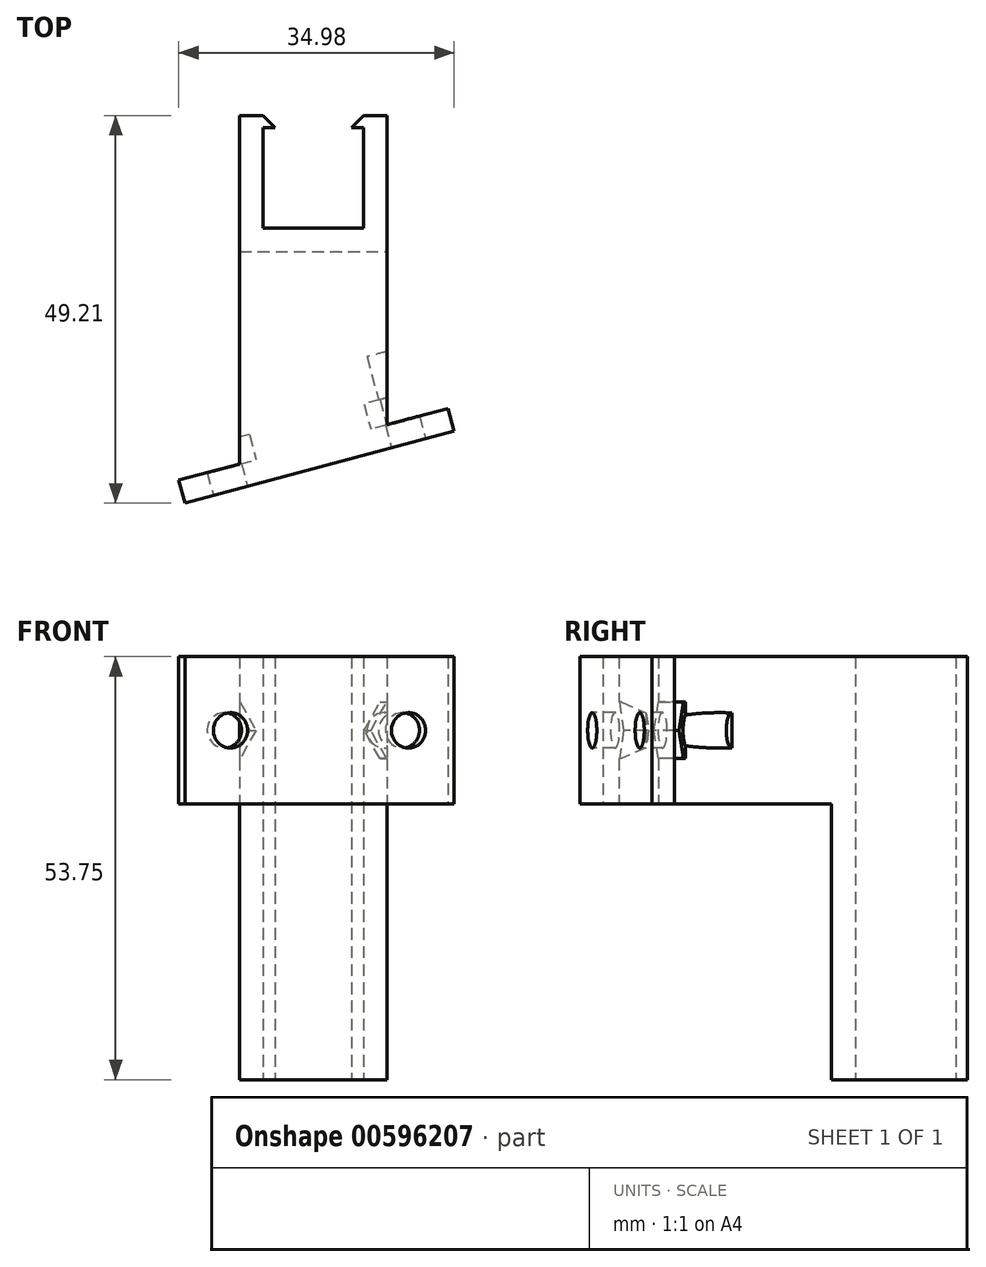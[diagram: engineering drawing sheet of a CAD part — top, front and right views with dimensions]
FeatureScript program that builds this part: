
annotation { "Feature Type Name" : "Feature", "Feature Type Description" : "" }
export const myFeature = defineFeature(function(context is Context, id is Id, definition is map)
    precondition{}
    {
        {
            assignVariable(context, id + "F0", {"name" : "bar", "anyValue" : 12.75});
        }
        {
            assignVariable(context, id + "F1", {"name" : "thickness", "anyValue" : 3});
        }
        {
            var Q0;
            Q0=qCreatedBy(makeId("Top.planeOp"),FACE);
            var sketch = newSketch(context, id + "F2", { "sketchPlane" : qUnion([Q0])});
            skLineSegment(sketch, "E0", {"start": v(-6.69, 24) * mm, "end": v(-6.69, 11.26) * mm});
            skLineSegment(sketch, "E1", {"start": v(-6.69, 11.26) * mm, "end": v(6.06, 11.26) * mm});
            skLineSegment(sketch, "E2", {"start": v(6.06, 11.26) * mm, "end": v(6.06, 24) * mm});
            skLineSegment(sketch, "E3", {"start": v(6.06, 24) * mm, "end": v(9.06, 24) * mm, "construction": true});
            skLineSegment(sketch, "E4", {"start": v(9.06, -13.74) * mm, "end": v(-9.69, -18.74) * mm});
            skLineSegment(sketch, "E5", {"start": v(-9.69, 24) * mm, "end": v(-6.69, 24) * mm, "construction": true});
            skLineSegment(sketch, "E6", {"start": v(6.06, 11.26) * mm, "end": v(9.06, 11.26) * mm, "construction": true});
            skLineSegment(sketch, "E7", {"start": v(-6.69, 11.26) * mm, "end": v(-9.69, 11.26) * mm, "construction": true});
            skLineSegment(sketch, "E8", {"start": v(9.06, 24) * mm, "end": v(9.06, 11.26) * mm});
            skLineSegment(sketch, "E9", {"start": v(9.06, 11.26) * mm, "end": v(9.06, -13.74) * mm});
            skLineSegment(sketch, "E10", {"start": v(-9.69, 11.26) * mm, "end": v(-9.69, -18.74) * mm});
            skLineSegment(sketch, "E11", {"start": v(-9.69, 11.26) * mm, "end": v(-9.69, 24) * mm});
            skLineSegment(sketch, "E12", {"start": v(-6.69, 24) * mm, "end": v(-5.19, 24) * mm});
            skLineSegment(sketch, "E13", {"start": v(-5.19, 24) * mm, "end": v(-6.69, 25.5) * mm});
            skLineSegment(sketch, "E14", {"start": v(-6.69, 25.5) * mm, "end": v(-9.69, 25.5) * mm});
            skLineSegment(sketch, "E15", {"start": v(-9.69, 25.5) * mm, "end": v(-9.69, 24) * mm});
            skLineSegment(sketch, "E16", {"start": v(6.06, 24) * mm, "end": v(4.56, 24) * mm});
            skLineSegment(sketch, "E17", {"start": v(4.56, 24) * mm, "end": v(6.06, 25.5) * mm});
            skLineSegment(sketch, "E18", {"start": v(6.06, 25.5) * mm, "end": v(9.06, 25.5) * mm});
            skLineSegment(sketch, "E19", {"start": v(9.06, 25.5) * mm, "end": v(9.06, 24) * mm});
            skSolve(sketch);
        }
        {
            var Q0;
            Q0=makeQuery(id+"F2.imprint","IMPRINT",FACE,{"disambiguationData":[TD([[makeQuery(id+"F2.imprint","IMPRINT",EDGE,{"derivedFrom":sQuery(id+"F2.wireOp",EDGE,"E0")}),-1.0]])]});
            extrude(context, id + "F3", {"entities" : qUnion([Q0]), "depth" : (2 * getVariable(context, 'thickness') + getVariable(context, 'bar')) * mm, "offsetDistance" : 25 * mm});
        }
        {
            var Q0;
            Q0=makeQuery(id+"F3.opExtrude","SWEPT_FACE",FACE,{"disambiguationData":[OSD([sQuery(id+"F2.wireOp",EDGE,"E4")])]});
            var sketch = newSketch(context, id + "F4", { "sketchPlane" : qUnion([Q0])});
            skLineSegment(sketch, "E20.bottom", {"start": v(-14.2, 18.75) * mm, "end": v(-22.2, 18.75) * mm});
            skLineSegment(sketch, "E20.top", {"start": v(-14.2, 0) * mm, "end": v(-22.2, 0) * mm});
            skLineSegment(sketch, "E20.left", {"start": v(-14.2, 18.75) * mm, "end": v(-14.2, 0) * mm});
            skLineSegment(sketch, "E20.right", {"start": v(-22.2, 18.75) * mm, "end": v(-22.2, 0) * mm});
            skLineSegment(sketch, "E21.bottom", {"start": v(5.21, 18.75) * mm, "end": v(13.21, 18.75) * mm});
            skLineSegment(sketch, "E21.top", {"start": v(5.21, 0) * mm, "end": v(13.21, 0) * mm});
            skLineSegment(sketch, "E21.left", {"start": v(5.21, 18.75) * mm, "end": v(5.21, 0) * mm});
            skLineSegment(sketch, "E21.right", {"start": v(13.21, 18.75) * mm, "end": v(13.21, 0) * mm});
            skLineSegment(sketch, "E22.bottom", {"start": v(5.21, 18.75) * mm, "end": v(-14.2, 18.75) * mm});
            skLineSegment(sketch, "E22.top", {"start": v(5.21, 0) * mm, "end": v(-14.2, 0) * mm});
            skSolve(sketch);
        }
        {
            var Q0;
            Q0=makeQuery(id+"F4.imprint","IMPRINT",FACE,{"disambiguationData":[TD([[makeQuery(id+"F4.imprint","IMPRINT",EDGE,{"derivedFrom":sQuery(id+"F4.wireOp",EDGE,"E22.bottom")}),1.0]])]});
            var Q1;
            Q1=makeQuery(id+"F4.imprint","IMPRINT",FACE,{"disambiguationData":[TD([[makeQuery(id+"F4.imprint","IMPRINT",EDGE,{"derivedFrom":sQuery(id+"F4.wireOp",EDGE,"E20.bottom")}),1.0]])]});
            var Q2;
            Q2=makeQuery(id+"F4.imprint","IMPRINT",FACE,{"disambiguationData":[TD([[makeQuery(id+"F4.imprint","IMPRINT",EDGE,{"derivedFrom":sQuery(id+"F4.wireOp",EDGE,"E21.bottom")}),-1.0]])]});
            extrude(context, id + "F5", {"entities" : qUnion([Q0, Q1, Q2]), "operationType" : NewBodyOperationType.ADD, "depth" : (getVariable(context, 'thickness')) * mm, "offsetDistance" : 25 * mm});
        }
        {
            var Q0;
            Q0=makeQuery(id+"F5.opExtrude","CAP_FACE",FACE,{"disambiguationData":[OSD([sQuery(id+"F4.wireOp",EDGE,"E20.bottom"),sQuery(id+"F4.wireOp",EDGE,"E20.top"),sQuery(id+"F4.wireOp",EDGE,"E20.right"),sQuery(id+"F4.wireOp",EDGE,"E21.bottom"),sQuery(id+"F4.wireOp",EDGE,"E21.top"),sQuery(id+"F4.wireOp",EDGE,"E21.right"),sQuery(id+"F4.wireOp",EDGE,"E22.bottom"),sQuery(id+"F4.wireOp",EDGE,"E22.top")])],"isStart":false});
            var sketch = newSketch(context, id + "F6", { "sketchPlane" : qUnion([Q0])});
            skCircle(sketch, "E23", {"center": v(-16.2, 9.37) * mm, "radius": 2.25 * mm});
            skCircle(sketch, "E24", {"center": v(7.21, 9.38) * mm, "radius": 2.25 * mm});
            skLineSegment(sketch, "E25", {"start": v(-22.2, 9.37) * mm, "end": v(-16.2, 9.37) * mm, "construction": true});
            skLineSegment(sketch, "E26", {"start": v(13.21, 9.38) * mm, "end": v(7.21, 9.38) * mm, "construction": true});
            skSolve(sketch);
        }
        {
            var Q0;
            Q0=makeQuery(id+"F6.imprint","IMPRINT",FACE,{"disambiguationData":[TD([[makeQuery(id+"F6.imprint","IMPRINT",EDGE,{"derivedFrom":sQuery(id+"F6.wireOp",EDGE,"E24")}),1.0]])]});
            var Q1;
            Q1=makeQuery(id+"F6.imprint","IMPRINT",FACE,{"disambiguationData":[TD([[makeQuery(id+"F6.imprint","IMPRINT",EDGE,{"derivedFrom":sQuery(id+"F6.wireOp",EDGE,"E23")}),1.0]])]});
            extrude(context, id + "F7", {"entities" : qUnion([Q0, Q1]), "operationType" : NewBodyOperationType.REMOVE, "oppositeDirection" : true, "depth" : 12 * mm, "offsetDistance" : 25 * mm});
        }
        {
            var Q0;
            Q0=makeQuery(id+"F4.imprint","IMPRINT",FACE,{"disambiguationData":[TD([[makeQuery(id+"F4.imprint","IMPRINT",EDGE,{"derivedFrom":sQuery(id+"F4.wireOp",EDGE,"E22.bottom")}),1.0]])]});
            var sketch = newSketch(context, id + "F8", { "sketchPlane" : qUnion([Q0])});
            skCircle(sketch, "E27.cCircle", {"center": v(7.21, 9.38) * mm, "radius": 3.6 * mm, "construction": true});
            skLineSegment(sketch, "E27.0", {"start": v(9.3, 5.78) * mm, "end": v(5.13, 5.78) * mm});
            skLineSegment(sketch, "E27.1", {"start": v(5.13, 5.77) * mm, "end": v(3.06, 9.37) * mm});
            skLineSegment(sketch, "E27.2", {"start": v(3.06, 9.37) * mm, "end": v(5.13, 12.97) * mm});
            skLineSegment(sketch, "E27.3", {"start": v(5.13, 12.97) * mm, "end": v(9.3, 12.97) * mm});
            skLineSegment(sketch, "E27.4", {"start": v(9.3, 12.97) * mm, "end": v(11.37, 9.37) * mm});
            skLineSegment(sketch, "E27.5", {"start": v(11.37, 9.38) * mm, "end": v(9.3, 5.78) * mm});
            skPoint(sketch, "E27.0.midPoint", {"position": v(7.21, 5.78) * mm});
            skCircle(sketch, "E28.cCircle", {"center": v(-16.2, 9.37) * mm, "radius": 3.6 * mm, "construction": true});
            skLineSegment(sketch, "E28.0", {"start": v(-14.11, 5.77) * mm, "end": v(-18.27, 5.77) * mm});
            skLineSegment(sketch, "E28.1", {"start": v(-18.27, 5.77) * mm, "end": v(-20.35, 9.37) * mm});
            skLineSegment(sketch, "E28.2", {"start": v(-20.35, 9.37) * mm, "end": v(-18.27, 12.98) * mm});
            skLineSegment(sketch, "E28.3", {"start": v(-18.27, 12.98) * mm, "end": v(-14.11, 12.98) * mm});
            skLineSegment(sketch, "E28.4", {"start": v(-14.11, 12.97) * mm, "end": v(-12.03, 9.37) * mm});
            skLineSegment(sketch, "E28.5", {"start": v(-12.03, 9.37) * mm, "end": v(-14.11, 5.77) * mm});
            skPoint(sketch, "E28.0.midPoint", {"position": v(-16.2, 5.77) * mm});
            skLineSegment(sketch, "E29.0.0", {"start": v(5.21, 18.75) * mm, "end": v(5.21, 0) * mm, "construction": true});
            skLineSegment(sketch, "E29.0.1", {"start": v(5.21, 0) * mm, "end": v(13.21, 0) * mm, "construction": true});
            skLineSegment(sketch, "E29.0.2", {"start": v(13.21, 0) * mm, "end": v(13.21, 18.75) * mm, "construction": true});
            skLineSegment(sketch, "E29.0.3", {"start": v(13.21, 18.75) * mm, "end": v(5.21, 18.75) * mm, "construction": true});
            skLineSegment(sketch, "E30.0.0", {"start": v(-22.2, 0) * mm, "end": v(-14.2, 0) * mm, "construction": true});
            skLineSegment(sketch, "E30.0.1", {"start": v(-14.2, 0) * mm, "end": v(-14.2, 18.75) * mm, "construction": true});
            skLineSegment(sketch, "E30.0.2", {"start": v(-14.2, 18.75) * mm, "end": v(-22.2, 18.75) * mm, "construction": true});
            skLineSegment(sketch, "E30.0.3", {"start": v(-22.2, 18.75) * mm, "end": v(-22.2, 0) * mm, "construction": true});
            skLineSegment(sketch, "E31", {"start": v(13.21, 9.38) * mm, "end": v(7.21, 9.38) * mm, "construction": true});
            skLineSegment(sketch, "E32", {"start": v(-22.2, 9.37) * mm, "end": v(-16.2, 9.37) * mm, "construction": true});
            skSolve(sketch);
        }
        {
            var Q0;
            {var subQ1=sQuery(id+"F8.wireOp",EDGE,"E27.4");Q0=makeQuery(id+"F8.imprint","IMPRINT",FACE,{"disambiguationData":[TD([[makeQuery(id+"F8.imprint","IMPRINT",EDGE,{"derivedFrom":subQ1}),-1.0]])]});}
            var Q1;
            {var subQ4=sQuery(id+"F8.wireOp",EDGE,"E27.1");Q1=makeQuery(id+"F8.imprint","IMPRINT",FACE,{"disambiguationData":[TD([[makeQuery(id+"F8.imprint","IMPRINT",EDGE,{"derivedFrom":subQ4}),-1.0]])]});}
            var Q2;
            {var subQ6=sQuery(id+"F8.wireOp",EDGE,"E28.1");Q2=makeQuery(id+"F8.imprint","IMPRINT",FACE,{"disambiguationData":[TD([[makeQuery(id+"F8.imprint","IMPRINT",EDGE,{"derivedFrom":subQ6}),-1.0]])]});}
            var Q3;
            {var subQ1=sQuery(id+"F8.wireOp",EDGE,"E28.4");Q3=makeQuery(id+"F8.imprint","IMPRINT",FACE,{"disambiguationData":[TD([[makeQuery(id+"F8.imprint","IMPRINT",EDGE,{"derivedFrom":subQ1}),-1.0]])]});}
            extrude(context, id + "F9", {"entities" : qUnion([Q0, Q1, Q2, Q3]), "operationType" : NewBodyOperationType.REMOVE, "oppositeDirection" : true, "depth" : 3.3 * mm, "offsetDistance" : 25 * mm});
        }
        {
            var Q0;
            Q0=makeQuery(id+"F5.boolean.opBoolean","MERGE",FACE,{"derivedFrom":[makeQuery(id+"F3.opExtrude","CAP_FACE",FACE,{"disambiguationData":[OSD([sQuery(id+"F2.wireOp",EDGE,"E0"),sQuery(id+"F2.wireOp",EDGE,"E1"),sQuery(id+"F2.wireOp",EDGE,"E2"),sQuery(id+"F2.wireOp",EDGE,"E4"),sQuery(id+"F2.wireOp",EDGE,"E8"),sQuery(id+"F2.wireOp",EDGE,"E9"),sQuery(id+"F2.wireOp",EDGE,"E10"),sQuery(id+"F2.wireOp",EDGE,"E11"),sQuery(id+"F2.wireOp",EDGE,"E12"),sQuery(id+"F2.wireOp",EDGE,"E13"),sQuery(id+"F2.wireOp",EDGE,"E14"),sQuery(id+"F2.wireOp",EDGE,"E15"),sQuery(id+"F2.wireOp",EDGE,"E16"),sQuery(id+"F2.wireOp",EDGE,"E17"),sQuery(id+"F2.wireOp",EDGE,"E18"),sQuery(id+"F2.wireOp",EDGE,"E19")])],"isStart":true}),makeQuery(id+"F5.opExtrude","SWEPT_FACE",FACE,{"disambiguationData":[OSD([sQuery(id+"F4.wireOp",EDGE,"E20.top"),sQuery(id+"F4.wireOp",EDGE,"E21.top"),sQuery(id+"F4.wireOp",EDGE,"E22.top")])]})]});
            var sketch = newSketch(context, id + "F10", { "sketchPlane" : qUnion([Q0])});
            skLineSegment(sketch, "E33", {"start": v(-9.69, -8.26) * mm, "end": v(9.06, -8.26) * mm});
            skLineSegment(sketch, "E34", {"start": v(-6.69, -11.26) * mm, "end": v(-6.69, -8.26) * mm, "construction": true});
            skSolve(sketch);
        }
        {
            var Q0;
            {var subQ2=sQuery(id+"F10.wireOp",EDGE,"E33");Q0=makeQuery(id+"F10.imprint","IMPRINT",FACE,{"disambiguationData":[TD([[makeQuery(id+"F10.imprint","IMPRINT",EDGE,{"derivedFrom":subQ2}),-1.0]])]});}
            extrude(context, id + "F11", {"entities" : qUnion([Q0]), "operationType" : NewBodyOperationType.ADD, "depth" : 35 * mm, "offsetDistance" : 25 * mm});
        }
    });
